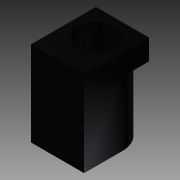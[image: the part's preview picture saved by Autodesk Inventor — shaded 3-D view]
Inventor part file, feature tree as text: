
AUTODESK INVENTOR PART (.ipt)
format: ipt  version: 2016 (Build 200138000, 138)  size: 97,792 bytes
history: native  units: mm
features: extrude x3, sketch x3
ambient origin geometry x8: Origin, YZ Plane, XZ Plane, XY Plane, X Axis, Y Axis, Z Axis, Center Point
bodies: Solid1 (feature_tree)
feature tree (6):
  extrude  "Extrusion1"  Depth=11.0mm
  extrude  "Extrusion2"  TaperAngle=0.0deg  [1 undecoded]
  extrude  "Extrusion3"  Depth=10.9mm TaperAngle=0.0deg
  sketch  "Sketch1"  dims[d0=9.0mm d1=11.0mm]
  sketch  "Sketch2"  dims[d2=0.0mm d3=0.0mm]
  sketch  "Sketch3"  dims[d4=3.5mm d5=0.0mm d6=10.9mm d7=0.0mm d8=6.5mm d9=6.5mm d10=10.9mm d11=0.0mm]
note: 1 required parameter value undecoded (feature->parameter linkage not recoverable at this tier; creation-order binding heuristic only, values carry confidence <= 0.55)
